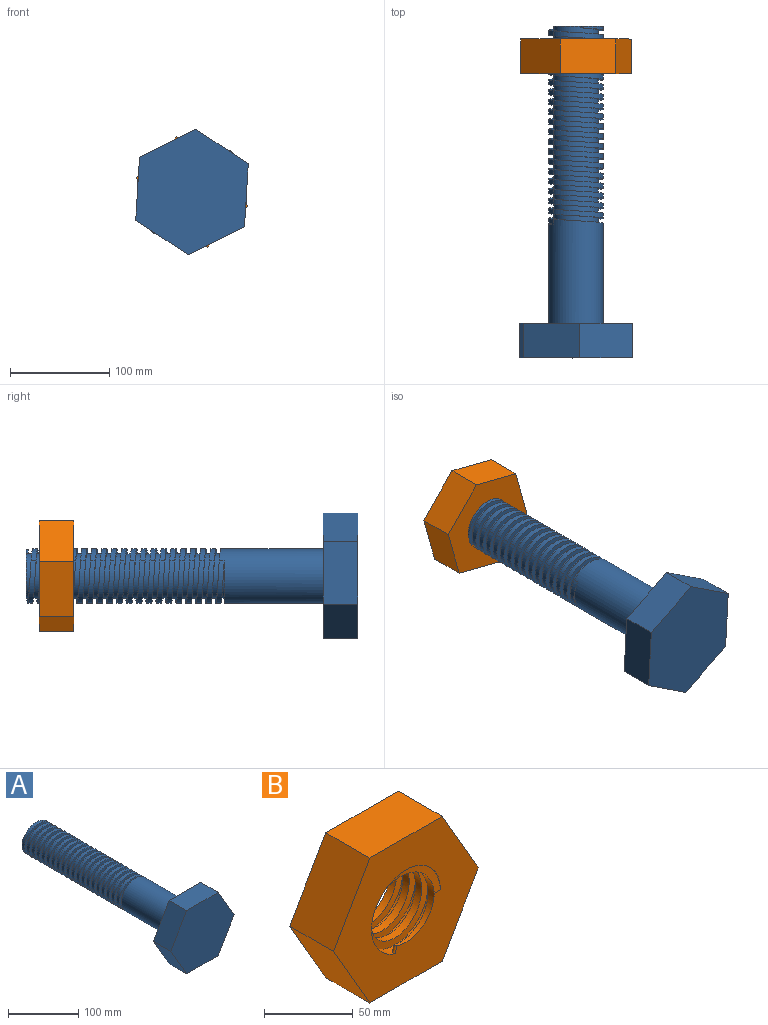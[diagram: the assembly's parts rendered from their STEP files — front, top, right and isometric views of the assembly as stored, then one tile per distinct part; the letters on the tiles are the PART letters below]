
ASSEMBLY  parts=2 mates=1
PART A: 35 faces, bbox 127x335x110 mm
  f0: plane 55x27.5mm, normal (0,1,0), area 392.7mm2, adj f21,f23,f24,f25
  f1: cylinder r=27.5mm len=55mm, axis (0,1,0), area 615mm2, adj f2,f22,f24,f25,f34
  f2: cylinder r=27.5mm len=55mm, axis (0,1,0), area 863.8mm2, adj f1,f3,f24,f25
  f3: cylinder r=27.5mm len=55mm, axis (0,1,0), area 864mm2, adj f2,f4,f24,f25
  f4: cylinder r=27.5mm len=55mm, axis (0,1,0), area 864mm2, adj f3,f5,f24,f25
  f5: cylinder r=27.5mm len=55mm, axis (0,1,0), area 864.3mm2, adj f4,f6,f24,f25
  f6: cylinder r=27.5mm len=55mm, axis (0,1,0), area 863.6mm2, adj f5,f7,f24,f25
  f7: cylinder r=27.5mm len=55mm, axis (0,1,0), area 864mm2, adj f6,f8,f24,f25
  f8: cylinder r=27.5mm len=55mm, axis (0,1,0), area 863.7mm2, adj f7,f9,f24,f25
  f9: cylinder r=27.5mm len=55mm, axis (0,1,0), area 864.3mm2, adj f8,f10,f24,f25
  f10: cylinder r=27.5mm len=55mm, axis (0,1,0), area 864mm2, adj f9,f11,f24,f25
  f11: cylinder r=27.5mm len=55mm, axis (0,1,0), area 863.8mm2, adj f10,f12,f24,f25
  f12: cylinder r=27.5mm len=55mm, axis (0,1,0), area 863.8mm2, adj f11,f13,f24,f25
  f13: cylinder r=27.5mm len=55mm, axis (0,1,0), area 863.8mm2, adj f12,f14,f24,f25
  f14: cylinder r=27.5mm len=55mm, axis (0,1,0), area 864.3mm2, adj f13,f15,f24,f25
  f15: cylinder r=27.5mm len=55mm, axis (0,1,0), area 863.9mm2, adj f14,f16,f24,f25
  f16: cylinder r=27.5mm len=55mm, axis (0,1,0), area 864mm2, adj f15,f17,f24,f25
  f17: cylinder r=27.5mm len=55mm, axis (0,1,0), area 863.5mm2, adj f16,f18,f24,f25
  f18: cylinder r=27.5mm len=55mm, axis (0,1,0), area 864.1mm2, adj f17,f19,f24,f25
  f19: cylinder r=27.5mm len=55mm, axis (0,1,0), area 864.1mm2, adj f18,f20,f24,f25
  f20: cylinder r=27.5mm len=55mm, axis (0,1,0), area 864.1mm2, adj f19,f21,f24,f25
  f21: cylinder r=27.5mm len=105mm, axis (0,1,0), area 17494.7mm2, adj f0,f20,f24,f33
  f22: plane 50x50mm, normal (0,1,0), area 1826.1mm2, adj f1,f23,f24,f34
  f23: cylinder r=22.5mm len=200mm, axis (0,1,0), area 15857.7mm2, adj f0,f22,f24,f25,f34
  f24: bspline ~201.25x55mm, area 15703mm2, adj f0,f1,f2,f3,f4,f5,f6,f7
  f25: bspline ~200x55mm, area 15579.5mm2, adj f0,f1,f2,f3,f4,f5,f6,f7
  f26: plane 55x35mm, normal (-0.87,0,-0.5), area 2222.8mm2, adj f27,f31,f32,f33
  f27: plane 63.51x35mm, normal (0,0,-1), area 2222.8mm2, adj f26,f28,f32,f33
  f28: plane 55x35mm, normal (0.87,0,-0.5), area 2222.8mm2, adj f27,f29,f32,f33
  f29: plane 55x35mm, normal (0.87,0,0.5), area 2222.8mm2, adj f28,f30,f32,f33
  f30: plane 63.51x35mm, normal (0,0,1), area 2222.8mm2, adj f29,f31,f32,f33
  f31: plane 55x35mm, normal (-0.87,0,0.5), area 2222.8mm2, adj f26,f30,f32,f33
  f32: plane 127.02x110mm, normal (0,-1,0), area 10478.9mm2, adj f26,f27,f28,f29,f30,f31
  f33: plane 127.02x110mm, normal (0,1,0), area 8103.1mm2, adj f21,f26,f27,f28,f29,f30,f31
  f34: bspline ~34.78x15.61mm, area 15.4mm2, adj f1,f22,f23,f25
PART B: 14 faces, bbox 115.5x36.3x100 mm
  f0: bspline ~55x55mm, area 2599.1mm2, adj f1,f3,f10,f12
  f1: cylinder r=22.5mm len=45mm, axis (0,-1,0), area 2425mm2, adj f0,f2,f3,f4,f12,f13
  f2: bspline ~55x55mm, area 2599.1mm2, adj f1,f4,f10,f13
  f3: plane 115.47x100mm, normal (0,-1,0), area 6520.1mm2, adj f0,f1,f5,f6,f7,f8,f9,f10
  f4: plane 115.47x100mm, normal (0,1,0), area 6520.1mm2, adj f1,f2,f5,f6,f7,f8,f9,f10
  f5: plane 50x35mm, normal (-0.87,0,-0.5), area 2020.7mm2, adj f3,f4,f6,f11
  f6: plane 57.74x35mm, normal (0,0,-1), area 2020.7mm2, adj f3,f4,f5,f7
  f7: plane 50x35mm, normal (0.87,0,-0.5), area 2020.7mm2, adj f3,f4,f6,f8
  f8: plane 50x35mm, normal (0.87,0,0.5), area 2020.7mm2, adj f3,f4,f7,f9
  f9: plane 57.74x35mm, normal (0,0,1), area 2020.7mm2, adj f3,f4,f8,f11
  f10: cylinder r=27.5mm len=55mm, axis (0,1,0), area 3084.3mm2, adj f0,f2,f3,f4,f12,f13
  f11: plane 50x35mm, normal (-0.87,0,0.5), area 2020.7mm2, adj f3,f4,f5,f9
  f12: bspline ~34.78x15.61mm, area 15.4mm2, adj f0,f1,f4,f10
  f13: bspline ~34.55x15.51mm, area 15.4mm2, adj f1,f2,f3,f10
PLACE A rot(axis=(0,-1,0),146.5deg) t=(78.26,2.76,338.11)mm
PLACE B rot(axis=(-0.8,0,0.6),180deg) t=(78.26,-45.31,338.11)mm fixed
MATE cylindrical B.f1 <-> A.f23  axis (0,1,0) through (78.26,-10.31,338.11)mm
